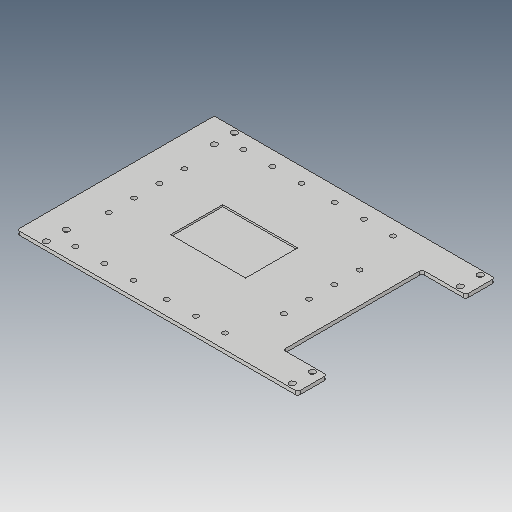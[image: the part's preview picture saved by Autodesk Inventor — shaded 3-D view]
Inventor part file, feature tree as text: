
AUTODESK INVENTOR PART (.ipt)
format: ipt  version: 2018 (Build 220112000, 112)  size: 197,120 bytes
history: native  units: mm
features: sketch x8, extrude x5, hole x3, mirror x3, plane x2, projected_geometry x2, fillet x1
ambient origin geometry x8: Origin, YZ Plane, XZ Plane, XY Plane, X Axis, Y Axis, Z Axis, Center Point
bodies: Solid1 (feature_tree)
feature tree (24):
  extrude  "Extrusion1"  Depth=172.0mm
  hole  "Hole1"  [1 undecoded]
  mirror  "Mirror1"
  extrude  "Extrusion2"  Depth=25.4mm TaperAngle=0.0deg
  extrude  "Extrusion3"  Depth=21.4376mm
  hole  "Hole2"  [1 undecoded]
  plane  "Work Plane2"
  mirror  "Mirror3"
  mirror  "Mirror4"
  hole  "Hole3"  [1 undecoded]
  extrude  "Extrusion4"  Depth=1.6mm TaperAngle=0.0deg
  fillet  "Fillet2"  Radius=25.4mm
  extrude  "Extrusion5"  Depth=121.2mm
  sketch  "Sketch1"  dims[d0=156.0mm d1=172.0mm]
  sketch  "Sketch2"  dims[d2=3.175mm d3=0.0mm d4=50.8mm]
  plane  "Work Plane1"
  sketch  "Sketch3"  dims[d5=12.7mm]
  projected_geometry  "Projected Loop1"
  sketch  "Sketch4"  dims[d7=4.5mm d8=6.0mm d9=9.4mm d10=2.0mm d11=90.0deg d12=8.0mm d13=20.594885mm d14=25.4mm d15=0.0mm]
  sketch  "Sketch5"  dims[d16=17.4625mm d17=21.4376mm]
  sketch  "Sketch6"  dims[d18=5.3mm d19=0.599mm d20=10.4mm d21=2.0mm d22=90.0deg d23=8.0mm d24=20.594885mm d26=66.0mm]
  projected_geometry  "Projected Loop2"
  sketch  "Sketch7"  dims[d28=4.5mm d29=6.0mm d30=9.4mm d31=2.0mm d32=90.0deg d33=8.0mm d34=20.594885mm d35=27.0mm]
  sketch  "Sketch8"  dims[d36=22.0mm d37=63.5mm d38=0.0mm d39=25.4mm d40=121.2mm d41=38.1mm d42=63.5mm d43=0.0mm d44=2.0mm d45=38.1mm d46=65.5mm d47=45.5mm d48=1.6mm d49=0.0mm]
note: 3 required parameter values undecoded (feature->parameter linkage not recoverable at this tier; creation-order binding heuristic only, values carry confidence <= 0.55)
